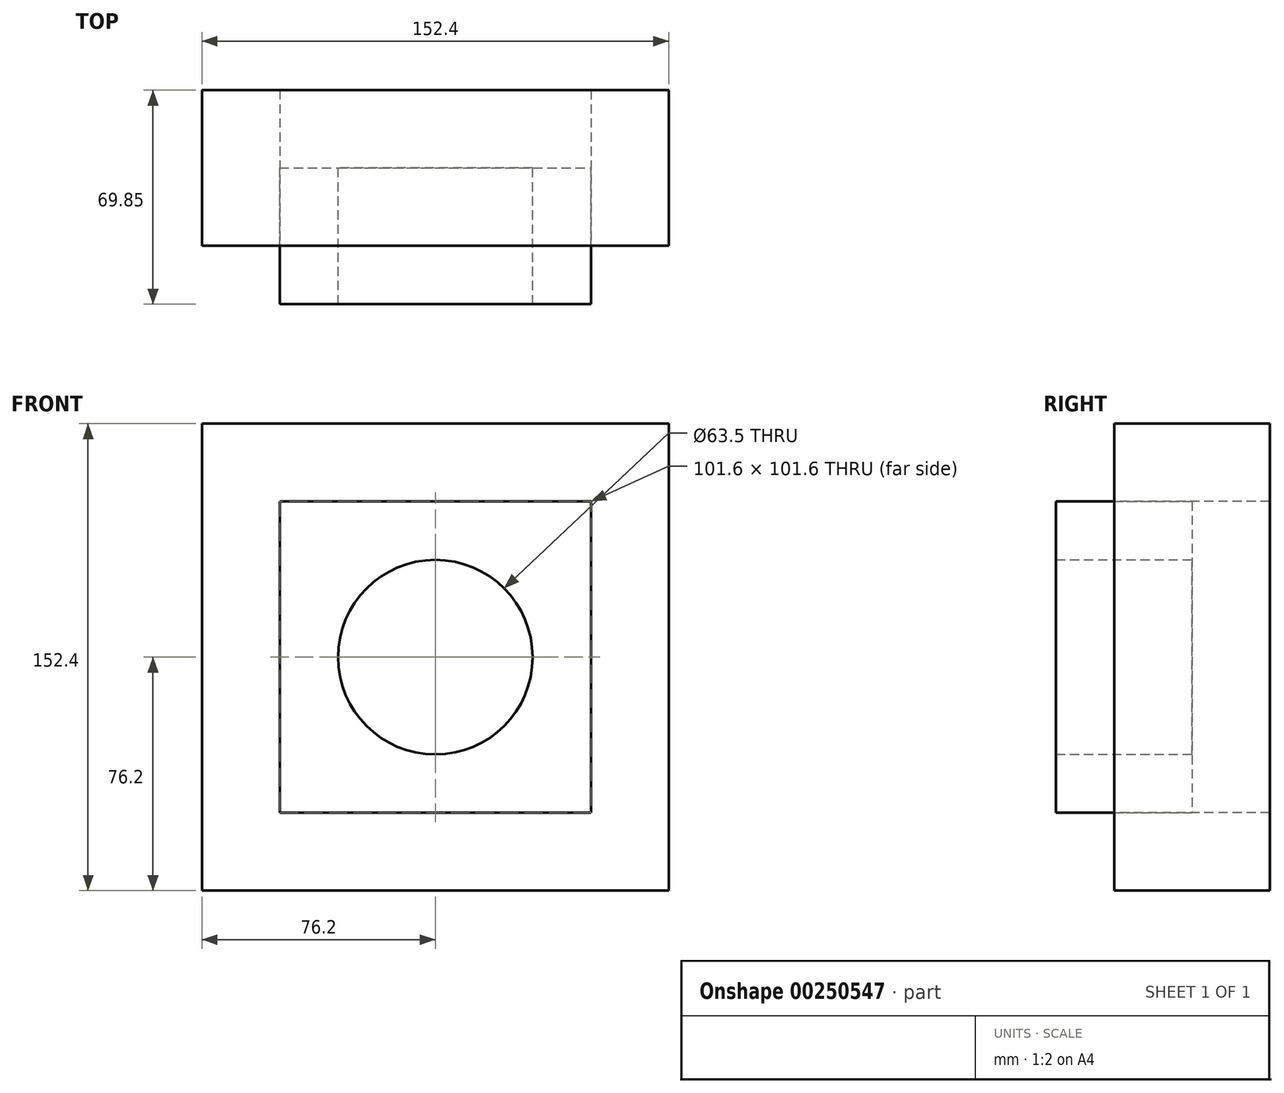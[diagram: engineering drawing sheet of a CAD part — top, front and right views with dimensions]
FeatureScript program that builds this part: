
annotation { "Feature Type Name" : "Feature", "Feature Type Description" : "" }
export const myFeature = defineFeature(function(context is Context, id is Id, definition is map)
    precondition{}
    {
        {
            var Q0;
            Q0=qCreatedBy(makeId("Front.planeOp"),FACE);
            var sketch = newSketch(context, id + "F0", { "sketchPlane" : qUnion([Q0])});
            skCircle(sketch, "E0", {"center": v(0, 0) * mm, "radius": 31.75 * mm});
            skLineSegment(sketch, "E1.bottom", {"start": v(-50.8, 50.8) * mm, "end": v(50.8, 50.8) * mm});
            skLineSegment(sketch, "E1.top", {"start": v(-50.8, -50.8) * mm, "end": v(50.8, -50.8) * mm});
            skLineSegment(sketch, "E1.left", {"start": v(-50.8, 50.8) * mm, "end": v(-50.8, -50.8) * mm});
            skLineSegment(sketch, "E1.right", {"start": v(50.8, 50.8) * mm, "end": v(50.8, -50.8) * mm});
            skLineSegment(sketch, "E2.bottom", {"start": v(-76.2, 76.2) * mm, "end": v(76.2, 76.2) * mm});
            skLineSegment(sketch, "E2.top", {"start": v(-76.2, -76.2) * mm, "end": v(76.2, -76.2) * mm});
            skLineSegment(sketch, "E2.left", {"start": v(-76.2, 76.2) * mm, "end": v(-76.2, -76.2) * mm});
            skLineSegment(sketch, "E2.right", {"start": v(76.2, 76.2) * mm, "end": v(76.2, -76.2) * mm});
            skSolve(sketch);
        }
        {
            var Q0;
            Q0=makeQuery(id+"F0.imprint","IMPRINT",FACE,{"disambiguationData":[TD([[makeQuery(id+"F0.imprint","IMPRINT",EDGE,{"derivedFrom":sQuery(id+"F0.wireOp",EDGE,"E0")}),-1.0]])]});
            extrude(context, id + "F1", {"entities" : qUnion([Q0]), "depth" : 44.45 * mm});
        }
        {
            var Q0;
            Q0 = qSketchRegion(id + "F0", true);
            extrude(context, id + "F2", {"entities" : qUnion([Q0]), "endBound" : BoundingType.SYMMETRIC, "oppositeDirection" : true, "depth" : 50.8 * mm});
        }
    });
